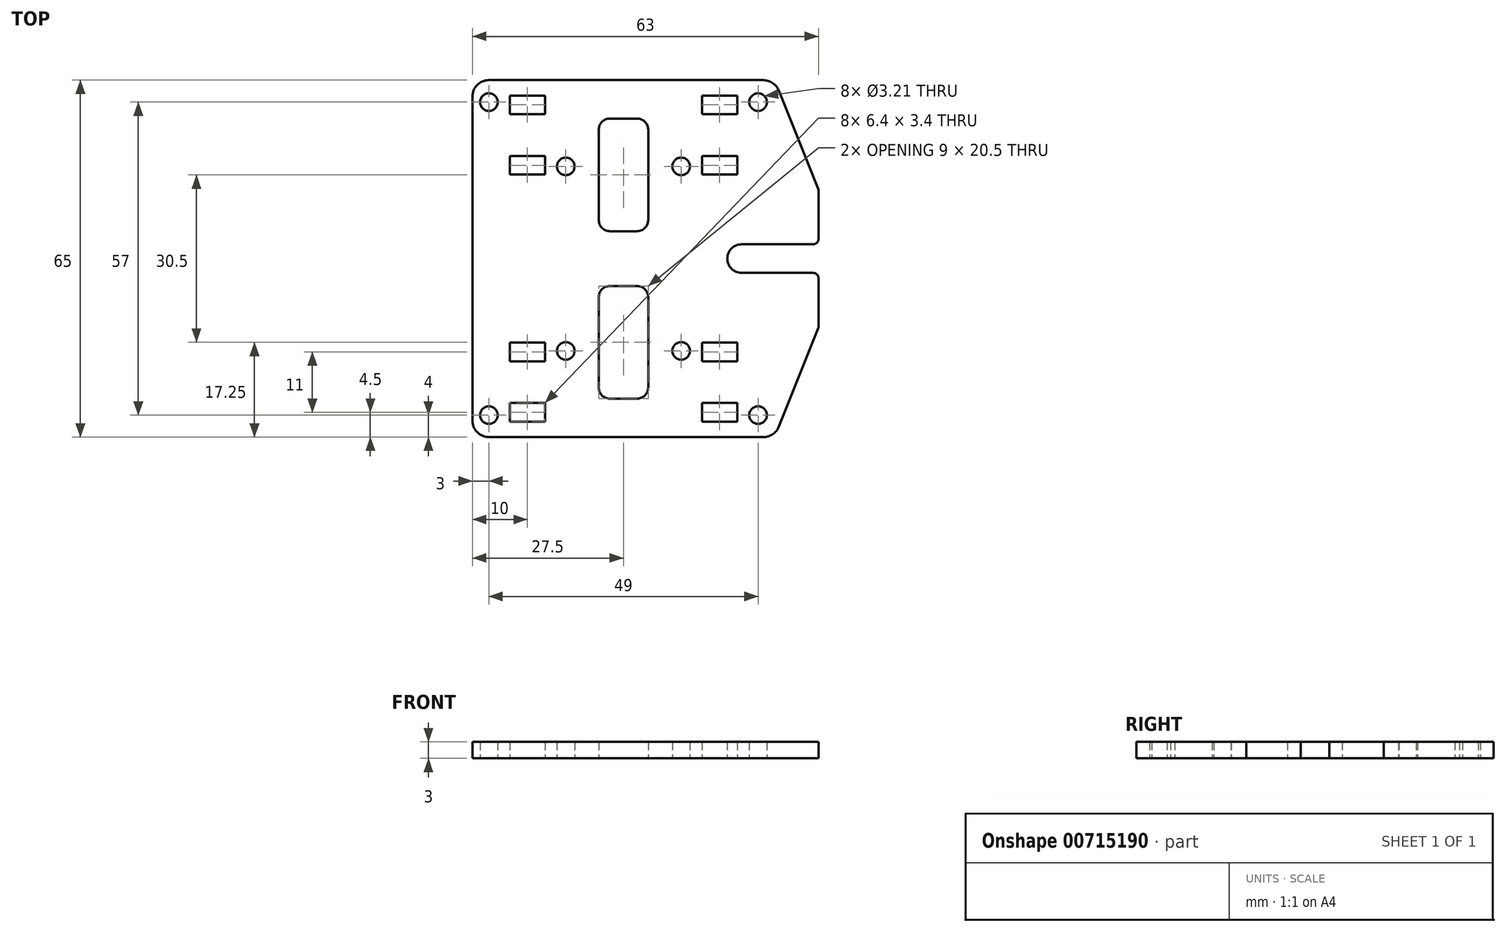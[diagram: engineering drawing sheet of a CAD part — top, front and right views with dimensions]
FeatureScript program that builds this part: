
annotation { "Feature Type Name" : "Feature", "Feature Type Description" : "" }
export const myFeature = defineFeature(function(context is Context, id is Id, definition is map)
    precondition{}
    {
        {
            var Q0;
            Q0=qCreatedBy(makeId("Top.planeOp"),FACE);
            var sketch = newSketch(context, id + "F0", { "sketchPlane" : qUnion([Q0])});
            skArc(sketch, "E0", {"start": v(0.5, 23.5) * mm, "mid": v(-0.09, 24.91) * mm, "end": v(-1.5, 25.5) * mm});
            skLineSegment(sketch, "E1", {"start": v(-6.5, 25.5) * mm, "end": v(-1.5, 25.5) * mm});
            skArc(sketch, "E2", {"start": v(-6.5, 25.5) * mm, "mid": v(-7.91, 24.91) * mm, "end": v(-8.5, 23.5) * mm});
            skArc(sketch, "E3", {"start": v(-1.5, -25.5) * mm, "mid": v(-0.09, -24.91) * mm, "end": v(0.5, -23.5) * mm});
            skLineSegment(sketch, "E4", {"start": v(-1.5, -25.5) * mm, "end": v(-6.5, -25.5) * mm});
            skArc(sketch, "E5", {"start": v(-8.5, -23.5) * mm, "mid": v(-7.91, -24.91) * mm, "end": v(-6.5, -25.5) * mm});
            skLineSegment(sketch, "E6", {"start": v(-8.5, 7) * mm, "end": v(-8.5, 23.5) * mm});
            skArc(sketch, "E7", {"start": v(-8.5, 7) * mm, "mid": v(-7.91, 5.59) * mm, "end": v(-6.5, 5) * mm});
            skLineSegment(sketch, "E8", {"start": v(0.5, 23.5) * mm, "end": v(0.5, 7) * mm});
            skLineSegment(sketch, "E9", {"start": v(-6.5, 5) * mm, "end": v(-1.5, 5) * mm});
            skArc(sketch, "E10", {"start": v(-1.5, 5) * mm, "mid": v(-0.09, 5.59) * mm, "end": v(0.5, 7) * mm});
            skLineSegment(sketch, "E11", {"start": v(-8.5, -23.5) * mm, "end": v(-8.5, -7) * mm});
            skArc(sketch, "E12", {"start": v(-6.5, -5) * mm, "mid": v(-7.91, -5.59) * mm, "end": v(-8.5, -7) * mm});
            skLineSegment(sketch, "E13", {"start": v(-6.5, -5) * mm, "end": v(-1.5, -5) * mm});
            skLineSegment(sketch, "E14", {"start": v(0.5, -7) * mm, "end": v(0.5, -23.5) * mm});
            skArc(sketch, "E15", {"start": v(0.5, -7) * mm, "mid": v(-0.09, -5.59) * mm, "end": v(-1.5, -5) * mm});
            skCircle(sketch, "E16", {"center": v(-14.5, 16.8) * mm, "radius": 1.6 * mm});
            skCircle(sketch, "E17", {"center": v(-28.5, -28.5) * mm, "radius": 1.6 * mm});
            skCircle(sketch, "E18", {"center": v(-28.5, 28.5) * mm, "radius": 1.6 * mm});
            skLineSegment(sketch, "E19", {"start": v(-18.3, 26.3) * mm, "end": v(-18.3, 29.7) * mm});
            skLineSegment(sketch, "E20", {"start": v(-18.3, 29.7) * mm, "end": v(-24.7, 29.7) * mm});
            skLineSegment(sketch, "E21", {"start": v(-18.3, 26.3) * mm, "end": v(-24.7, 26.3) * mm});
            skLineSegment(sketch, "E22", {"start": v(-24.7, 29.7) * mm, "end": v(-24.7, 26.3) * mm});
            skLineSegment(sketch, "E23", {"start": v(-18.3, 15.3) * mm, "end": v(-18.3, 18.7) * mm});
            skLineSegment(sketch, "E24", {"start": v(-18.3, 18.7) * mm, "end": v(-24.7, 18.7) * mm});
            skLineSegment(sketch, "E25", {"start": v(-18.3, 15.3) * mm, "end": v(-24.7, 15.3) * mm});
            skLineSegment(sketch, "E26", {"start": v(-24.7, 18.7) * mm, "end": v(-24.7, 15.3) * mm});
            skLineSegment(sketch, "E27", {"start": v(-18.3, -18.7) * mm, "end": v(-18.3, -15.3) * mm});
            skLineSegment(sketch, "E28", {"start": v(-18.3, -15.3) * mm, "end": v(-24.7, -15.3) * mm});
            skLineSegment(sketch, "E29", {"start": v(-18.3, -18.7) * mm, "end": v(-24.7, -18.7) * mm});
            skLineSegment(sketch, "E30", {"start": v(-24.7, -15.3) * mm, "end": v(-24.7, -18.7) * mm});
            skLineSegment(sketch, "E31", {"start": v(-18.3, -29.7) * mm, "end": v(-18.3, -26.3) * mm});
            skLineSegment(sketch, "E32", {"start": v(-18.3, -26.3) * mm, "end": v(-24.7, -26.3) * mm});
            skLineSegment(sketch, "E33", {"start": v(-18.3, -29.7) * mm, "end": v(-24.7, -29.7) * mm});
            skLineSegment(sketch, "E34", {"start": v(-24.7, -26.3) * mm, "end": v(-24.7, -29.7) * mm});
            skCircle(sketch, "E35", {"center": v(20.5, 28.5) * mm, "radius": 1.6 * mm});
            skCircle(sketch, "E36", {"center": v(6.5, 16.8) * mm, "radius": 1.6 * mm});
            skCircle(sketch, "E37", {"center": v(20.5, -28.5) * mm, "radius": 1.6 * mm});
            skLineSegment(sketch, "E38", {"start": v(16.7, 26.3) * mm, "end": v(16.7, 29.7) * mm});
            skLineSegment(sketch, "E39", {"start": v(16.7, 29.7) * mm, "end": v(10.3, 29.7) * mm});
            skLineSegment(sketch, "E40", {"start": v(16.7, 26.3) * mm, "end": v(10.3, 26.3) * mm});
            skLineSegment(sketch, "E41", {"start": v(10.3, 29.7) * mm, "end": v(10.3, 26.3) * mm});
            skLineSegment(sketch, "E42", {"start": v(16.7, 15.3) * mm, "end": v(16.7, 18.7) * mm});
            skLineSegment(sketch, "E43", {"start": v(16.7, 18.7) * mm, "end": v(10.3, 18.7) * mm});
            skLineSegment(sketch, "E44", {"start": v(16.7, 15.3) * mm, "end": v(10.3, 15.3) * mm});
            skLineSegment(sketch, "E45", {"start": v(10.3, 18.7) * mm, "end": v(10.3, 15.3) * mm});
            skLineSegment(sketch, "E46", {"start": v(16.7, -18.7) * mm, "end": v(16.7, -15.3) * mm});
            skLineSegment(sketch, "E47", {"start": v(16.7, -15.3) * mm, "end": v(10.3, -15.3) * mm});
            skLineSegment(sketch, "E48", {"start": v(16.7, -18.7) * mm, "end": v(10.3, -18.7) * mm});
            skLineSegment(sketch, "E49", {"start": v(10.3, -15.3) * mm, "end": v(10.3, -18.7) * mm});
            skLineSegment(sketch, "E50", {"start": v(16.7, -29.7) * mm, "end": v(16.7, -26.3) * mm});
            skLineSegment(sketch, "E51", {"start": v(16.7, -26.3) * mm, "end": v(10.3, -26.3) * mm});
            skLineSegment(sketch, "E52", {"start": v(16.7, -29.7) * mm, "end": v(10.3, -29.7) * mm});
            skLineSegment(sketch, "E53", {"start": v(10.3, -26.3) * mm, "end": v(10.3, -29.7) * mm});
            skCircle(sketch, "E54", {"center": v(-14.5, -16.8) * mm, "radius": 1.6 * mm});
            skCircle(sketch, "E55", {"center": v(6.5, -16.8) * mm, "radius": 1.6 * mm});
            skArc(sketch, "E56", {"start": v(17.5, 2.6) * mm, "mid": v(14.9, 0) * mm, "end": v(17.5, -2.6) * mm});
            skLineSegment(sketch, "E57", {"start": v(31.5, 12.5) * mm, "end": v(31.5, 3.6) * mm});
            skLineSegment(sketch, "E58", {"start": v(17.5, 2.6) * mm, "end": v(30.5, 2.6) * mm});
            skArc(sketch, "E59", {"start": v(30.5, 2.6) * mm, "mid": v(31.2, 2.9) * mm, "end": v(31.5, 3.6) * mm});
            skLineSegment(sketch, "E60", {"start": v(17.5, -2.6) * mm, "end": v(30.5, -2.6) * mm});
            skLineSegment(sketch, "E61", {"start": v(31.5, -12.5) * mm, "end": v(31.5, -3.6) * mm});
            skArc(sketch, "E62", {"start": v(31.5, -3.6) * mm, "mid": v(31.2, -2.9) * mm, "end": v(30.5, -2.6) * mm});
            skArc(sketch, "E63", {"start": v(24.25, 30.61) * mm, "mid": v(23.15, 31.98) * mm, "end": v(21.47, 32.5) * mm});
            skLineSegment(sketch, "E64", {"start": v(31.5, -12.5) * mm, "end": v(24.25, -30.61) * mm});
            skArc(sketch, "E65", {"start": v(21.47, -32.5) * mm, "mid": v(23.15, -31.98) * mm, "end": v(24.25, -30.61) * mm});
            skLineSegment(sketch, "E66", {"start": v(21.47, -32.5) * mm, "end": v(-28.5, -32.5) * mm});
            skArc(sketch, "E67", {"start": v(-31.5, -29.5) * mm, "mid": v(-30.62, -31.62) * mm, "end": v(-28.5, -32.5) * mm});
            skLineSegment(sketch, "E68", {"start": v(21.47, 32.5) * mm, "end": v(-28.5, 32.5) * mm});
            skArc(sketch, "E69", {"start": v(-28.5, 32.5) * mm, "mid": v(-30.62, 31.62) * mm, "end": v(-31.5, 29.5) * mm});
            skLineSegment(sketch, "E70", {"start": v(24.25, 30.61) * mm, "end": v(31.5, 12.5) * mm});
            skLineSegment(sketch, "E71", {"start": v(-31.5, 29.5) * mm, "end": v(-31.5, -29.5) * mm});
            skSolve(sketch);
        }
        {
            var Q0;
            Q0 = qSketchRegion(id + "F0", true);
            extrude(context, id + "F1", {"entities" : qUnion([Q0]), "depth" : 3 * mm, "offsetDistance" : 25 * mm});
        }
    });
